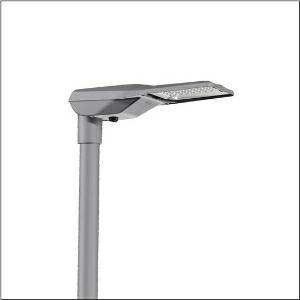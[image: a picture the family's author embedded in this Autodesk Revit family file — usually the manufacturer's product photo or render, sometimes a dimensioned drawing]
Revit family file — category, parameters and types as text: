
# Revit family: streetlight_sl_21_mini___st1_0ab_5xe2m33r08hb_9a5f
name_source: partatom
category: Lighting Fixtures
units: mm (PartAtom-declared; Revit-internal decimal feet)

## family parameters
Cut with Voids When Loaded = No
Host = Face
Light Source = No
Part Type = Normal
Room Calculation Point = No
Round Connector Dimension = Use Diameter
Shared = No

## types (1)
- --- (1 x LED, 7960 lm, 66 W, 3000K)
    Apparent Load = 66 VA
    CIE Flux Codes = 38 73 97 100 100
    Color Rendering = 70
    Color Temperature = 3000K
    Default Elevation = 1800 mm
    Description = Streetlight SL 21 mini, mast luminaire, primary light control with lens, of PMMA, primary optical cover: cover, of toughened safety glass, transparent, light distribution: ST1.0aB, light emission: direct distribution, primary light characteristic: asymmetric, installation type: side-entry, post-top, LED, High Power LED, rated luminous flux: 7.960lm, luminous efficacy: 121lm/W, light colour: 730, colour temperature: 3000K, control gear: D4i, control: flexible luminous flux parameterisation, time-dependent luminous flux control, constant luminous flux control, overheat protection, pre-setting: logarithmic dimming characteristic, mains connection: 220..240V, AC, 50/60Hz, start of lifetime: 66W, end of service life: 69W, reduction: 30W, luminaire housing, of diecast aluminium, powder-coated, Siteco® metallic grey (DB 702S), corrosivity category C5 mid according to DIN EN ISO 12944, please order mast flange separately, inclination adjustable: 0°, 5°, 10°, 15°, sealing non-destructively replaceable, multi-level sealing system, length: 628mm, width: 235mm, height: 110mm, mast flange for spigot size: 42mm (side-entry): 5XC10008XM4, 60/48mm (side-entry/post-top): 5XC10108XM2, 76/60mm (side-entry/post-top): 5XC10108XM1, mounting height: 4..8m, Smart Interface below, protection rating (complete): IP66, insulation class (complete): insulation class II (safety insulation), certification: CE, ENEC, ENEC+, VDE, impact resistance: IK10, permissible operating ambient temperature for outdoor applications: -40..+50°C, standard-compliant lighting for roads and squares, packaging unit: 1 piece

Light Distribution: ST1.0aB
    Height = 110 mm
    Lamp = 1 x LED
    Lamp Light Flux = 7960 lm
    Lamp Power = 66 W
    Lamp count = 1
    Length = 625 mm
    Luminous efficacy = 121 lm/W
    Manufacturer = Siteco
    ModVariant = No
    Model = 5XE2M33R08HB
    Number of Poles = 1
    OnlyDefault = Yes
    Power Factor = 1
    Product Name = Streetlight SL 21 mini | ST1.0aB
    Product group = mast luminaire | pylon top
    ProductGroupID = 6100
    Protection Class = Protection class II
    Protection Degree = IP 66
    RLX_Detail_Level = 1
    RLX_Emergency_Light_Flux = 0 lm
    RLX_Emergency_Type = 0
    RLX_Emergency_Type_DB = No
    RlxData = <blob elided: 26193 chars, md5=a437854f>
    Socket = socket
    Standby Power = 0 W
    System Light Flux = 7960 lm
    System Power = 66 W
    Type Comments = factory setting: luminous flux: 100 % | dim-lin: 254 | 670 mA
    Type Image = l_1003516.jpg
    URL = http://relux.com
    VarID = @adj_203955
    Voltage = 0 V
    Weight = 0.00 kg
    Width = 234 mm

## geometry (parser evidence)
native form markers: Blend x4, Sweep x10
no freeform markers — native parametric forms only
